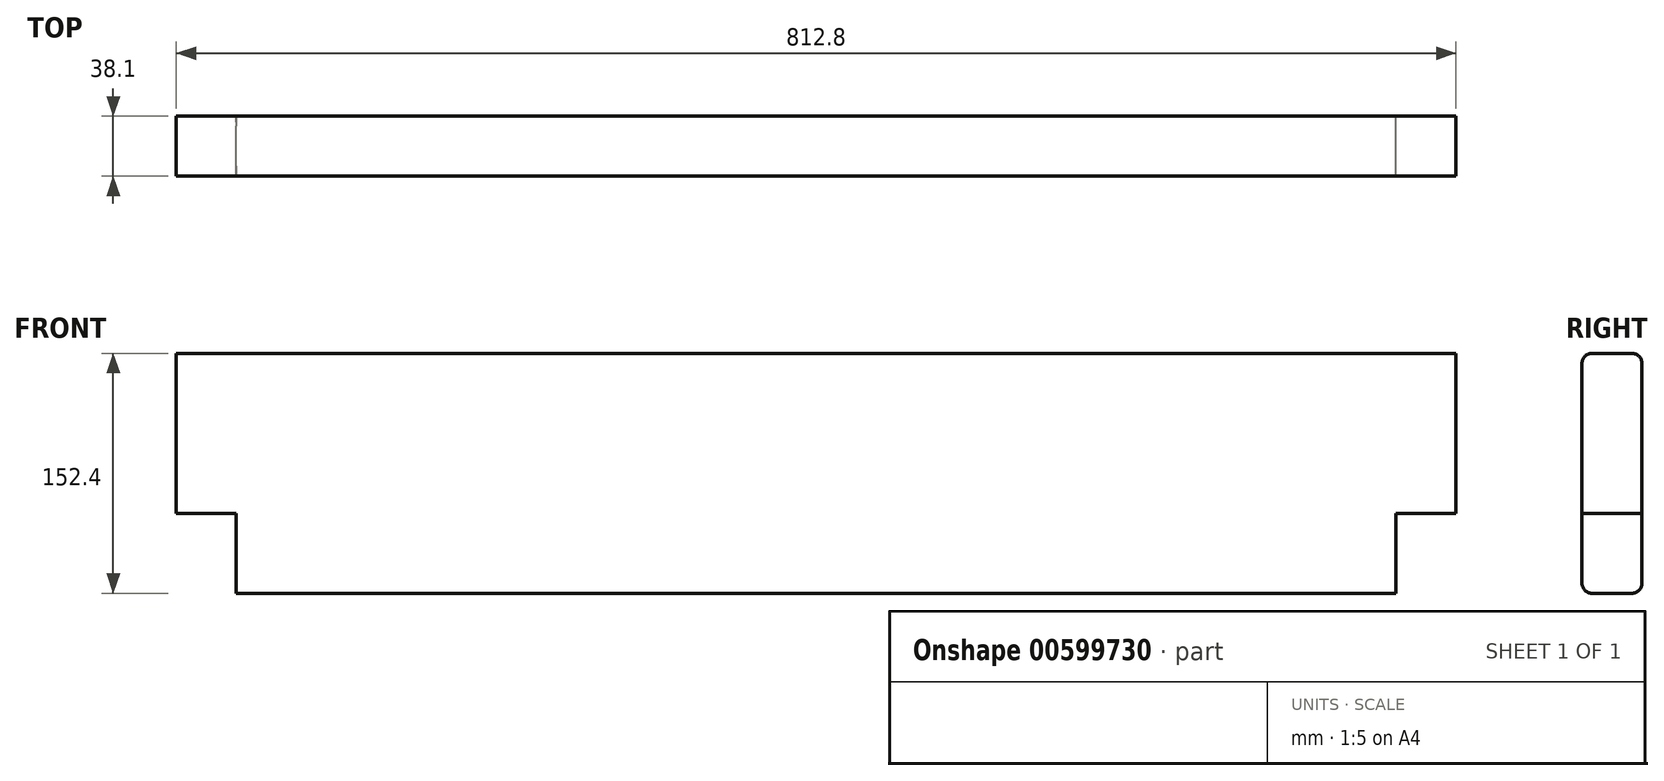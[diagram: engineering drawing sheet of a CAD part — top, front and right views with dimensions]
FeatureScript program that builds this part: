
annotation { "Feature Type Name" : "Feature", "Feature Type Description" : "" }
export const myFeature = defineFeature(function(context is Context, id is Id, definition is map)
    precondition{}
    {
        {
            var Q0;
            Q0=qCreatedBy(makeId("Front.planeOp"),FACE);
            var sketch = newSketch(context, id + "F0", { "sketchPlane" : qUnion([Q0])});
            skLineSegment(sketch, "E0", {"start": v(0, 0) * mm, "end": v(812.8, 0) * mm});
            skLineSegment(sketch, "E1", {"start": v(812.8, 0) * mm, "end": v(812.8, -101.6) * mm});
            skLineSegment(sketch, "E2", {"start": v(812.8, -101.6) * mm, "end": v(774.7, -101.6) * mm});
            skLineSegment(sketch, "E3", {"start": v(774.7, -101.6) * mm, "end": v(774.7, -152.4) * mm});
            skLineSegment(sketch, "E4", {"start": v(774.7, -152.4) * mm, "end": v(38.1, -152.4) * mm});
            skLineSegment(sketch, "E5", {"start": v(38.1, -152.4) * mm, "end": v(38.1, -101.6) * mm});
            skLineSegment(sketch, "E6", {"start": v(38.1, -101.6) * mm, "end": v(0, -101.6) * mm});
            skLineSegment(sketch, "E7", {"start": v(0, -101.6) * mm, "end": v(0, 0) * mm});
            skSolve(sketch);
        }
        {
            var Q0;
            Q0=makeQuery(id+"F0.imprint","IMPRINT",FACE,{"disambiguationData":[TD([[makeQuery(id+"F0.imprint","IMPRINT",EDGE,{"derivedFrom":sQuery(id+"F0.wireOp",EDGE,"E0")}),-1.0]])]});
            extrude(context, id + "F1", {"entities" : qUnion([Q0]), "depth" : 38.1 * mm, "offsetDistance" : 25.4 * mm});
        }
        {
            var Q0;
            Q0=makeQuery(id+"F1.opExtrude","CAP_EDGE",EDGE,{"disambiguationData":[OSD([sQuery(id+"F0.wireOp",EDGE,"E0")])],"isStart":false});
            var Q1;
            Q1=makeQuery(id+"F1.opExtrude","CAP_EDGE",EDGE,{"disambiguationData":[OSD([sQuery(id+"F0.wireOp",EDGE,"E4")])],"isStart":false});
            var Q2;
            Q2=makeQuery(id+"F1.opExtrude","CAP_EDGE",EDGE,{"disambiguationData":[OSD([sQuery(id+"F0.wireOp",EDGE,"E0")])],"isStart":true});
            var Q3;
            Q3=makeQuery(id+"F1.opExtrude","CAP_EDGE",EDGE,{"disambiguationData":[OSD([sQuery(id+"F0.wireOp",EDGE,"E4")])],"isStart":true});
            fillet(context, id + "F2", {"entities" : qUnion([Q0, Q1, Q2, Q3]), "radius" : 6.35 * mm, "tangentPropagation" : true, "allowEdgeOverflow" : false});
        }
    });
